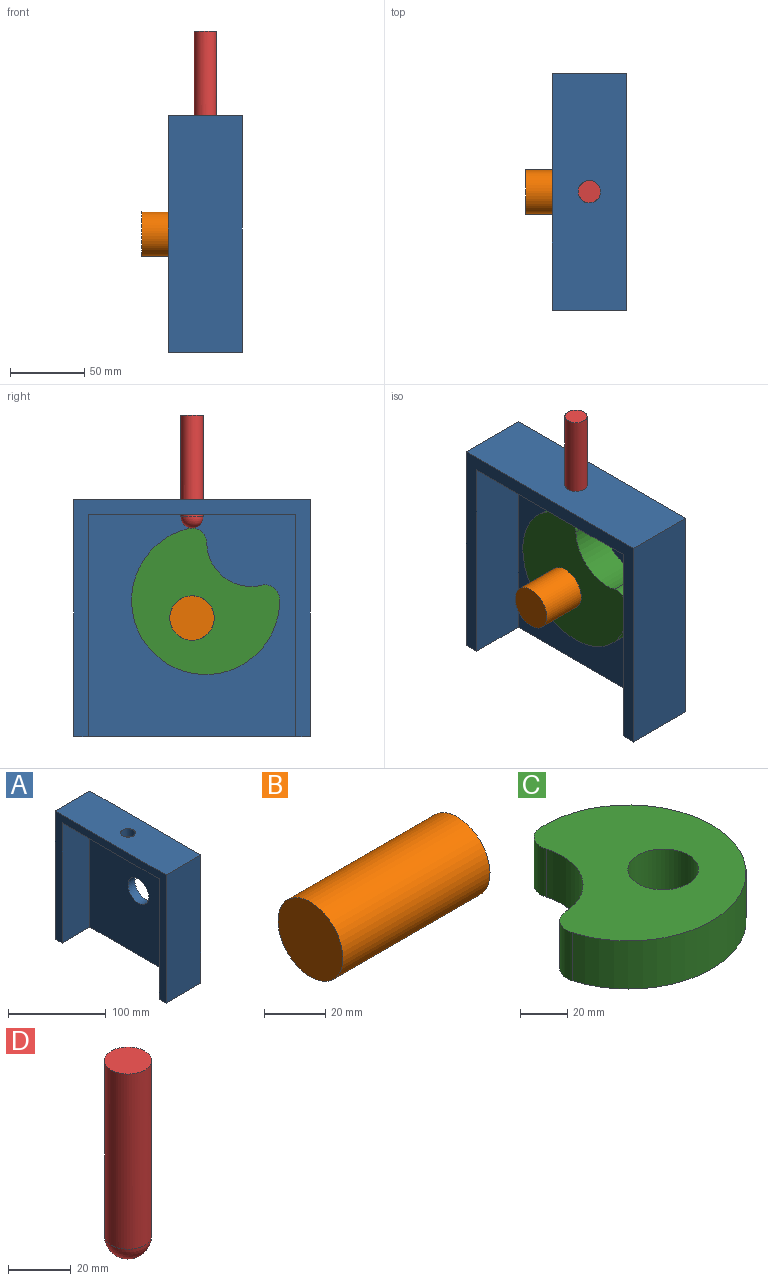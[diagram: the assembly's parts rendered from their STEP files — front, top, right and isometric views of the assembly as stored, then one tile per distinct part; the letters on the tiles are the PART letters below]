
ASSEMBLY  parts=4 mates=4
PART A: 12 faces, bbox 50x160x160 mm
  f0: plane 160x160mm, normal (-1,0,0), area 4600mm2, adj f1,f2,f3,f4,f6,f7,f8
  f1: plane 160x50mm, normal (0,0,1), area 7823.3mm2, adj f0,f2,f4,f5,f11
  f2: plane 160x50mm, normal (0,-1,0), area 8000mm2, adj f0,f1,f3,f5
  f3: plane 160x50mm, normal (0,0,-1), area 2400mm2, adj f0,f2,f4,f5,f7,f8,f9
  f4: plane 160x50mm, normal (0,1,0), area 8000mm2, adj f0,f1,f3,f5
  f5: plane 160x160mm, normal (1,0,0), area 24893.1mm2, adj f1,f2,f3,f4,f10
  f6: plane 140x40mm, normal (0,0,-1), area 5423.3mm2, adj f0,f7,f8,f9,f11
  f7: plane 150x40mm, normal (0,1,0), area 6000mm2, adj f0,f3,f6,f9
  f8: plane 150x40mm, normal (0,-1,0), area 6000mm2, adj f0,f3,f6,f9
  f9: plane 150x140mm, normal (-1,0,0), area 20293.1mm2, adj f3,f6,f7,f8,f10
  f10: cylinder r=15mm len=30mm, axis (-1,0,0), area 942.5mm2, adj f5,f9
  f11: cylinder r=7.5mm len=15mm, axis (0,0,1), area 471.2mm2, adj f1,f6
PART B: 3 faces, bbox 68x30x30 mm
  f0: cylinder r=15mm len=68mm, axis (-1,0,0), area 6408.8mm2, adj f1,f2
  f1: plane 30x30mm, normal (1,0,0), area 706.9mm2, adj f0
  f2: plane 30x30mm, normal (-1,0,0), area 706.9mm2, adj f0
PART C: 7 faces, bbox 98.4x100x25 mm
  f0: cylinder r=50mm len=100mm, axis (0,0,-1), area 5614.8mm2, adj f3,f4,f5,f6
  f1: cylinder r=15mm len=30mm, axis (0,0,-1), area 2356.2mm2, adj f3,f4
  f2: cylinder r=30mm len=38.41mm, axis (0,0,-1), area 1343.5mm2, adj f3,f4,f5,f6
  f3: plane 100x98.37mm, normal (0,0,1), area 5842.2mm2, adj f0,f1,f2,f5,f6
  f4: plane 100x98.37mm, normal (0,0,-1), area 5842.2mm2, adj f0,f1,f2,f5,f6
  f5: cylinder r=10mm len=25mm, axis (0,0,1), area 447.8mm2, adj f0,f2,f3,f4
  f6: cylinder r=10mm len=25mm, axis (0,0,1), area 447.8mm2, adj f0,f2,f3,f4
PART D: 3 faces, bbox 15x15x76 mm
  f0: cylinder r=7.5mm len=68.5mm, axis (0,0,-1), area 3228mm2, adj f1,f2
  f1: plane 15x15mm, normal (0,0,1), area 176.7mm2, adj f0
  f2: sphere r=7.5mm, area 353.4mm2, adj f0
PLACE A t=(34,-4.97,-0.79)mm fixed
PLACE B t=(16,-4.97,-0.79)mm
PLACE C rot(axis=(0.51,0.69,0.51),110.6deg) t=(49,-14.18,-68.96)mm
PLACE D rot(axis=(0,0,1),6.6deg) t=(34.17,-7.86,17.95)mm
MATE cylindrical C.f1 <-> B.f0  axis (-1,0,0) through (49,-4.97,-80.79)mm
MATE revolute B.f0 <-> A.f10  axis (-1,0,0) through (84,-4.97,-80.79)mm
MATE planar C.f3 <-> A.f9  axis (1,0,0) through (74,-10.38,-73.84)mm
MATE cylindrical D.f0 <-> A.f11  axis (0,0,-1) through (59,-4.97,21.7)mm
